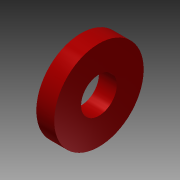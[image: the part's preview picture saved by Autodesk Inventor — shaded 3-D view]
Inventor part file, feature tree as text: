
AUTODESK INVENTOR PART (.ipt)
format: ipt  version: 2013 (Build 170138000, 138)  size: 77,824 bytes
history: native  units: mm
features: other x1, extrude x1, sketch x1
ambient origin geometry x8: Origin, YZ Plane, XZ Plane, XY Plane, X Axis, Y Axis, Z Axis, Center Point
feature tree (3):
  other  "ソリッド1"
  extrude  "押し出し1"  Depth=2.0mm
  sketch  "スケッチ1"
